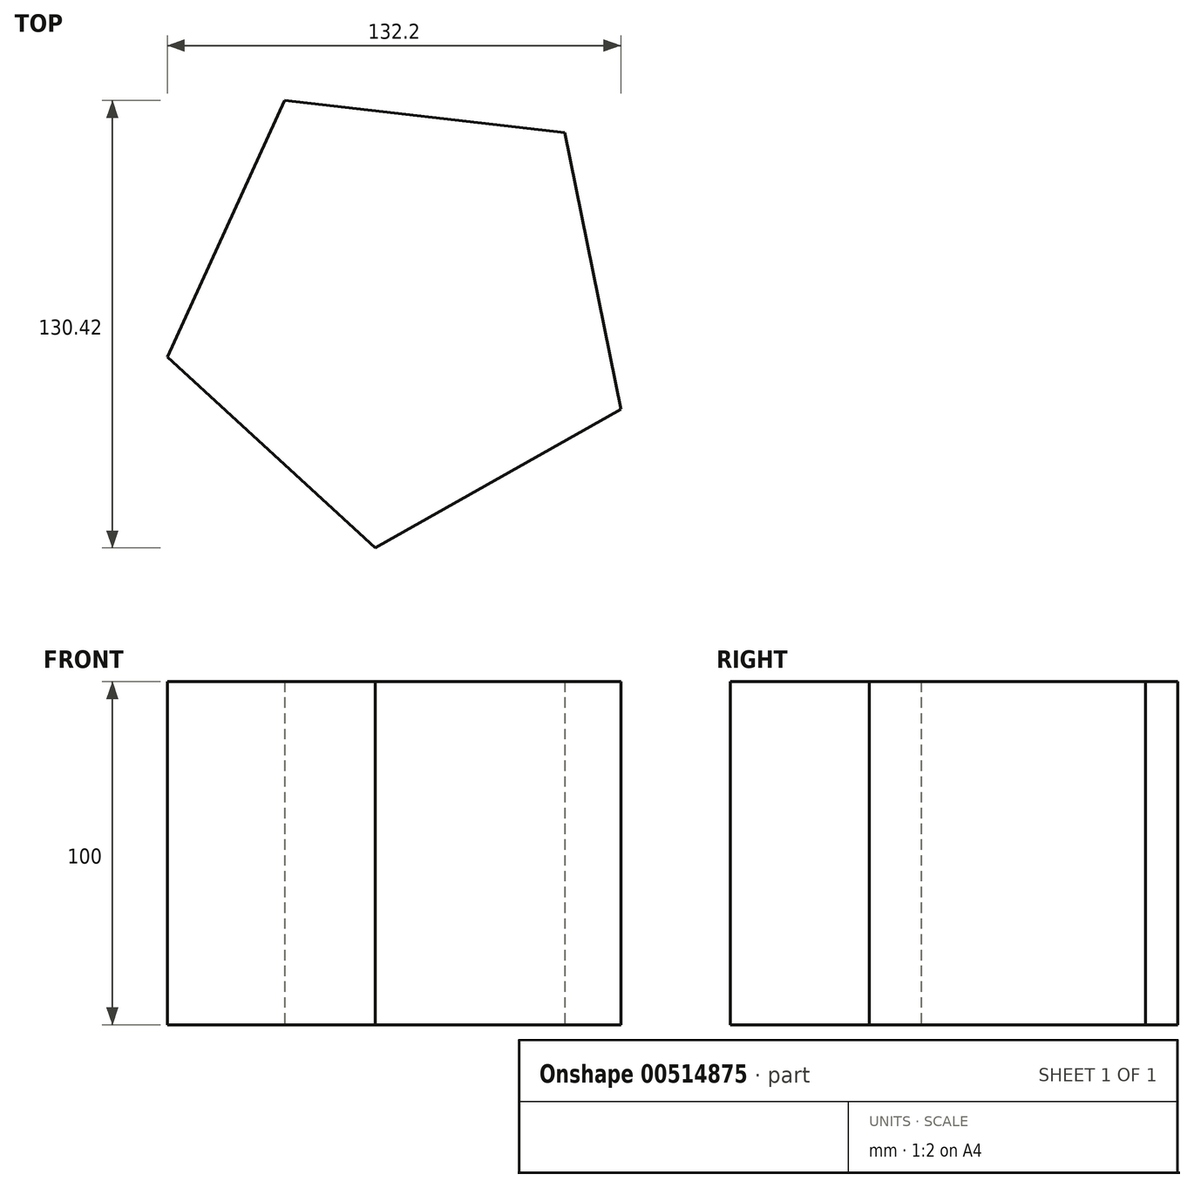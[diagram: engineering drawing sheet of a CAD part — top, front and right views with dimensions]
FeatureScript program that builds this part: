
annotation { "Feature Type Name" : "Feature", "Feature Type Description" : "" }
export const myFeature = defineFeature(function(context is Context, id is Id, definition is map)
    precondition{}
    {
        {
            var Q0;
            Q0=qCreatedBy(makeId("Top.planeOp"),FACE);
            var sketch = newSketch(context, id + "F0", { "sketchPlane" : qUnion([Q0])});
            skCircle(sketch, "E0.cCircle", {"center": v(5.54, -11.22) * mm, "radius": 69.96 * mm, "construction": true});
            skLineSegment(sketch, "E0.0", {"start": v(-28.86, 49.7) * mm, "end": v(52.85, 40.31) * mm});
            skLineSegment(sketch, "E0.1", {"start": v(52.85, 40.31) * mm, "end": v(69.17, -40.29) * mm});
            skLineSegment(sketch, "E0.2", {"start": v(69.17, -40.29) * mm, "end": v(-2.44, -80.72) * mm});
            skLineSegment(sketch, "E0.3", {"start": v(-2.44, -80.72) * mm, "end": v(-63.03, -25.1) * mm});
            skLineSegment(sketch, "E0.4", {"start": v(-63.03, -25.1) * mm, "end": v(-28.86, 49.7) * mm});
            skSolve(sketch);
        }
        {
            var Q0;
            Q0=makeQuery(id+"F0.imprint","IMPRINT",FACE,{"disambiguationData":[TD([[makeQuery(id+"F0.imprint","IMPRINT",EDGE,{"derivedFrom":sQuery(id+"F0.wireOp",EDGE,"E0.0")}),-1.0]])]});
            extrude(context, id + "F1", {"entities" : qUnion([Q0]), "depth" : 100 * mm, "offsetDistance" : 25.4 * mm});
        }
    });
